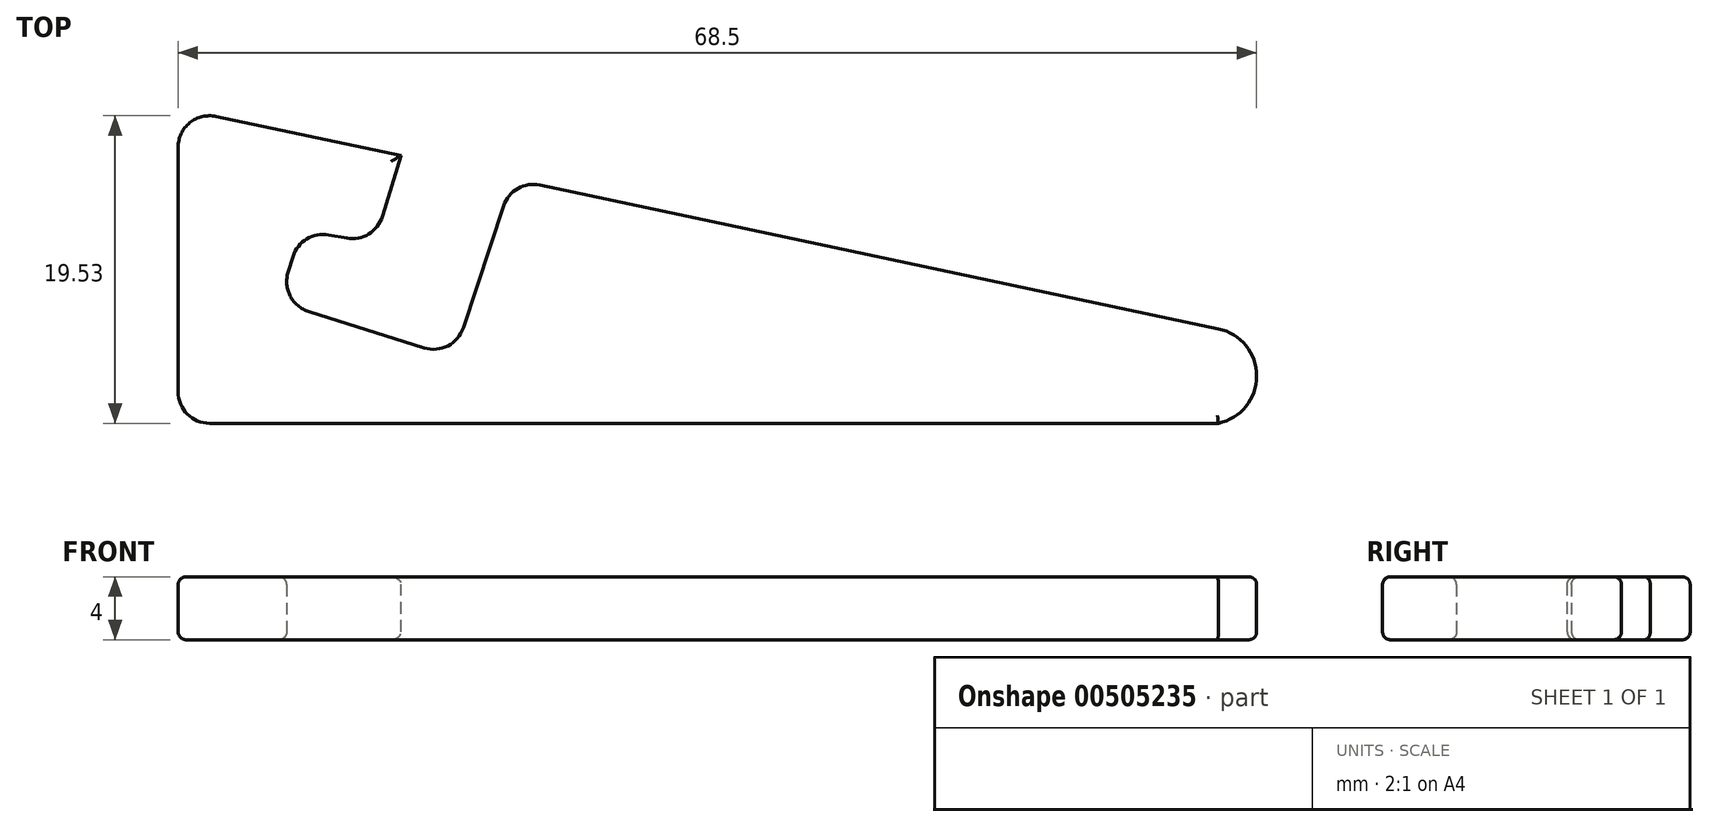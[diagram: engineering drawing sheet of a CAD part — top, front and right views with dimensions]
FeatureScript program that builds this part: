
annotation { "Feature Type Name" : "Feature", "Feature Type Description" : "" }
export const myFeature = defineFeature(function(context is Context, id is Id, definition is map)
    precondition{}
    {
        {
            var Q0;
            Q0=qCreatedBy(makeId("Top.planeOp"),FACE);
            var sketch = newSketch(context, id + "F0", { "sketchPlane" : qUnion([Q0])});
            skLineSegment(sketch, "E0", {"start": v(0, 0) * mm, "end": v(0, 20) * mm});
            skLineSegment(sketch, "E1", {"start": v(0, 20) * mm, "end": v(66.07, 6) * mm});
            skLineSegment(sketch, "E2", {"start": v(0, 0) * mm, "end": v(66.07, 0) * mm});
            skLineSegment(sketch, "E3", {"start": v(68.5, 0) * mm, "end": v(68.5, 20) * mm, "construction": true});
            skArc(sketch, "E4", {"start": v(66.07, 0) * mm, "mid": v(68.5, 3) * mm, "end": v(66.07, 6) * mm});
            skSolve(sketch);
        }
        {
            var Q0;
            Q0=makeQuery(id+"F0.imprint","IMPRINT",FACE,{"disambiguationData":[TD([[makeQuery(id+"F0.imprint","IMPRINT",EDGE,{"derivedFrom":sQuery(id+"F0.wireOp",EDGE,"E0")}),-1.0]])]});
            extrude(context, id + "F1", {"entities" : qUnion([Q0]), "depth" : 4 * mm, "offsetDistance" : 25 * mm});
        }
        {
            var Q0;
            Q0=makeQuery(id+"F1.opExtrude","CAP_FACE",FACE,{"disambiguationData":[OSD([sQuery(id+"F0.wireOp",EDGE,"E0"),sQuery(id+"F0.wireOp",EDGE,"E1"),sQuery(id+"F0.wireOp",EDGE,"E2"),sQuery(id+"F0.wireOp",EDGE,"E4")])],"isStart":false});
            var sketch = newSketch(context, id + "F2", { "sketchPlane" : qUnion([Q0])});
            skLineSegment(sketch, "E5", {"start": v(14.16, 17) * mm, "end": v(12.46, 11.45) * mm});
            skLineSegment(sketch, "E6", {"start": v(12.46, 11.45) * mm, "end": v(7.83, 12.27) * mm});
            skLineSegment(sketch, "E7", {"start": v(7.83, 12.27) * mm, "end": v(6.39, 7.7) * mm});
            skLineSegment(sketch, "E8", {"start": v(6.39, 7.7) * mm, "end": v(17.5, 4.2) * mm});
            skLineSegment(sketch, "E9", {"start": v(17.5, 4.2) * mm, "end": v(21.24, 15.5) * mm});
            skLineSegment(sketch, "E10", {"start": v(6.39, 7.7) * mm, "end": v(0, 0) * mm, "construction": true});
            skLineSegment(sketch, "E11", {"start": v(0, 20) * mm, "end": v(7.83, 12.27) * mm, "construction": true});
            skLineSegment(sketch, "E12", {"start": v(17.5, 4.2) * mm, "end": v(17.5, 0) * mm, "construction": true});
            skLineSegment(sketch, "E13", {"start": v(21.24, 15.5) * mm, "end": v(21.24, 0) * mm, "construction": true});
            skLineSegment(sketch, "E14", {"start": v(14.16, 17) * mm, "end": v(14.16, 0) * mm, "construction": true});
            skLineSegment(sketch, "E15", {"start": v(14.16, 17) * mm, "end": v(21.24, 15.5) * mm});
            skSolve(sketch);
        }
        {
            var Q0;
            Q0 = qSketchRegion(id + "F2", true);
            extrude(context, id + "F3", {"entities" : qUnion([Q0]), "operationType" : NewBodyOperationType.REMOVE, "endBound" : BoundingType.THROUGH_ALL, "oppositeDirection" : true, "depth" : 25 * mm, "offsetDistance" : 25 * mm});
        }
        {
            var Q0;
            Q0=makeQuery(id+"F1.opExtrude","SWEPT_EDGE",EDGE,{"disambiguationData":[OSD([sQuery(id+"F0.wireOp",EDGE,"E0"),sQuery(id+"F0.wireOp",EDGE,"E1")])]});
            var Q1;
            Q1=makeQuery(id+"F1.opExtrude","SWEPT_EDGE",EDGE,{"disambiguationData":[OSD([sQuery(id+"F0.wireOp",EDGE,"E0"),sQuery(id+"F0.wireOp",EDGE,"E2")])]});
            var Q2;
            Q2=makeQuery(id+"F3.boolean.opBoolean","COPY",EDGE,{"derivedFrom":makeQuery(id+"F3.opExtrude","SWEPT_EDGE",EDGE,{"disambiguationData":[OSD([sQuery(id+"F0.wireOp",EDGE,"E1"),sQuery(id+"F2.wireOp",EDGE,"E5"),sQuery(id+"F2.wireOp",EDGE,"E15")])]})});
            var Q3;
            Q3=makeQuery(id+"F3.boolean.opBoolean","COPY",EDGE,{"derivedFrom":makeQuery(id+"F3.opExtrude","SWEPT_EDGE",EDGE,{"disambiguationData":[OSD([sQuery(id+"F0.wireOp",EDGE,"E1"),sQuery(id+"F2.wireOp",EDGE,"E9"),sQuery(id+"F2.wireOp",EDGE,"E15")])]})});
            var Q4;
            Q4=makeQuery(id+"F3.boolean.opBoolean","COPY",EDGE,{"derivedFrom":makeQuery(id+"F3.opExtrude","SWEPT_EDGE",EDGE,{"disambiguationData":[OSD([sQuery(id+"F2.wireOp",EDGE,"E8"),sQuery(id+"F2.wireOp",EDGE,"E9")])]})});
            var Q5;
            Q5=makeQuery(id+"F3.boolean.opBoolean","COPY",EDGE,{"derivedFrom":makeQuery(id+"F3.opExtrude","SWEPT_EDGE",EDGE,{"disambiguationData":[OSD([sQuery(id+"F2.wireOp",EDGE,"E7"),sQuery(id+"F2.wireOp",EDGE,"E8")])]})});
            var Q6;
            Q6=makeQuery(id+"F3.boolean.opBoolean","COPY",EDGE,{"derivedFrom":makeQuery(id+"F3.opExtrude","SWEPT_EDGE",EDGE,{"disambiguationData":[OSD([sQuery(id+"F2.wireOp",EDGE,"E6"),sQuery(id+"F2.wireOp",EDGE,"E7")])]})});
            var Q7;
            Q7=makeQuery(id+"F3.boolean.opBoolean","COPY",EDGE,{"derivedFrom":makeQuery(id+"F3.opExtrude","SWEPT_EDGE",EDGE,{"disambiguationData":[OSD([sQuery(id+"F2.wireOp",EDGE,"E5"),sQuery(id+"F2.wireOp",EDGE,"E6")])]})});
            fillet(context, id + "F4", {"entities" : qUnion([Q0, Q1, Q2, Q3, Q4, Q5, Q6, Q7]), "radius" : 2 * mm, "tangentPropagation" : true, "allowEdgeOverflow" : false});
        }
        {
            var Q0;
            Q0=makeQuery(id+"F1.opExtrude","CAP_FACE",FACE,{"disambiguationData":[OSD([sQuery(id+"F0.wireOp",EDGE,"E0"),sQuery(id+"F0.wireOp",EDGE,"E1"),sQuery(id+"F0.wireOp",EDGE,"E2"),sQuery(id+"F0.wireOp",EDGE,"E4")])],"isStart":false});
            var Q1;
            Q1=makeQuery(id+"F1.opExtrude","CAP_FACE",FACE,{"disambiguationData":[OSD([sQuery(id+"F0.wireOp",EDGE,"E0"),sQuery(id+"F0.wireOp",EDGE,"E1"),sQuery(id+"F0.wireOp",EDGE,"E2"),sQuery(id+"F0.wireOp",EDGE,"E4")])],"isStart":true});
            fillet(context, id + "F5", {"entities" : qUnion([Q0, Q1]), "radius" : 0.5 * mm, "tangentPropagation" : true, "allowEdgeOverflow" : false});
        }
    });
